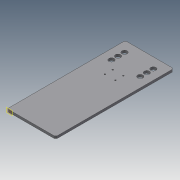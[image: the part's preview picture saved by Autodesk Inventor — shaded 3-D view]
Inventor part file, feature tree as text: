
AUTODESK INVENTOR PART (.ipt)
format: ipt  version: 2014 SP1 (Build 180222100, 222)  size: 119,808 bytes
history: native  units: in
note: dims shown in document units (in); Inventor stores cm internally (conversion verified against a paired STEP export)
features: extrude x2, sketch x2, plane x1, chamfer x1
ambient origin geometry x8: Origin, YZ Plane, XZ Plane, XY Plane, X Axis, Y Axis, Z Axis, Center Point
bodies: Solid1 (feature_tree)
feature tree (6):
  plane  "Work Plane1"
  extrude  "Extrusion1"  Depth=11.2726in TaperAngle=0.0deg
  extrude  "Extrusion2"  Depth=0.2228in
  chamfer  "Chamfer1"  Distance=3.0in
  sketch  "Sketch1"  dims[d0=0.2228in d2=11.2726in d3=0.0in]
  sketch  "Sketch2"  dims[d4=1.0in d5=0.75in d6=3.0in d7=0.5in d8=0.125in d9=0.125in d10=0.125in d11=0.125in d12=0.5in d13=0.5in d14=0.625in d15=1.0in d16=0.5in d17=0.625in d18=0.5in d19=0.5in d20=0.5in d21=0.625in d22=0.625in d23=1.0in d24=1.375in d25=1.375in d26=0.2228in d27=0.0in d28=0.125in d29=0.125in d30=45.0deg]
